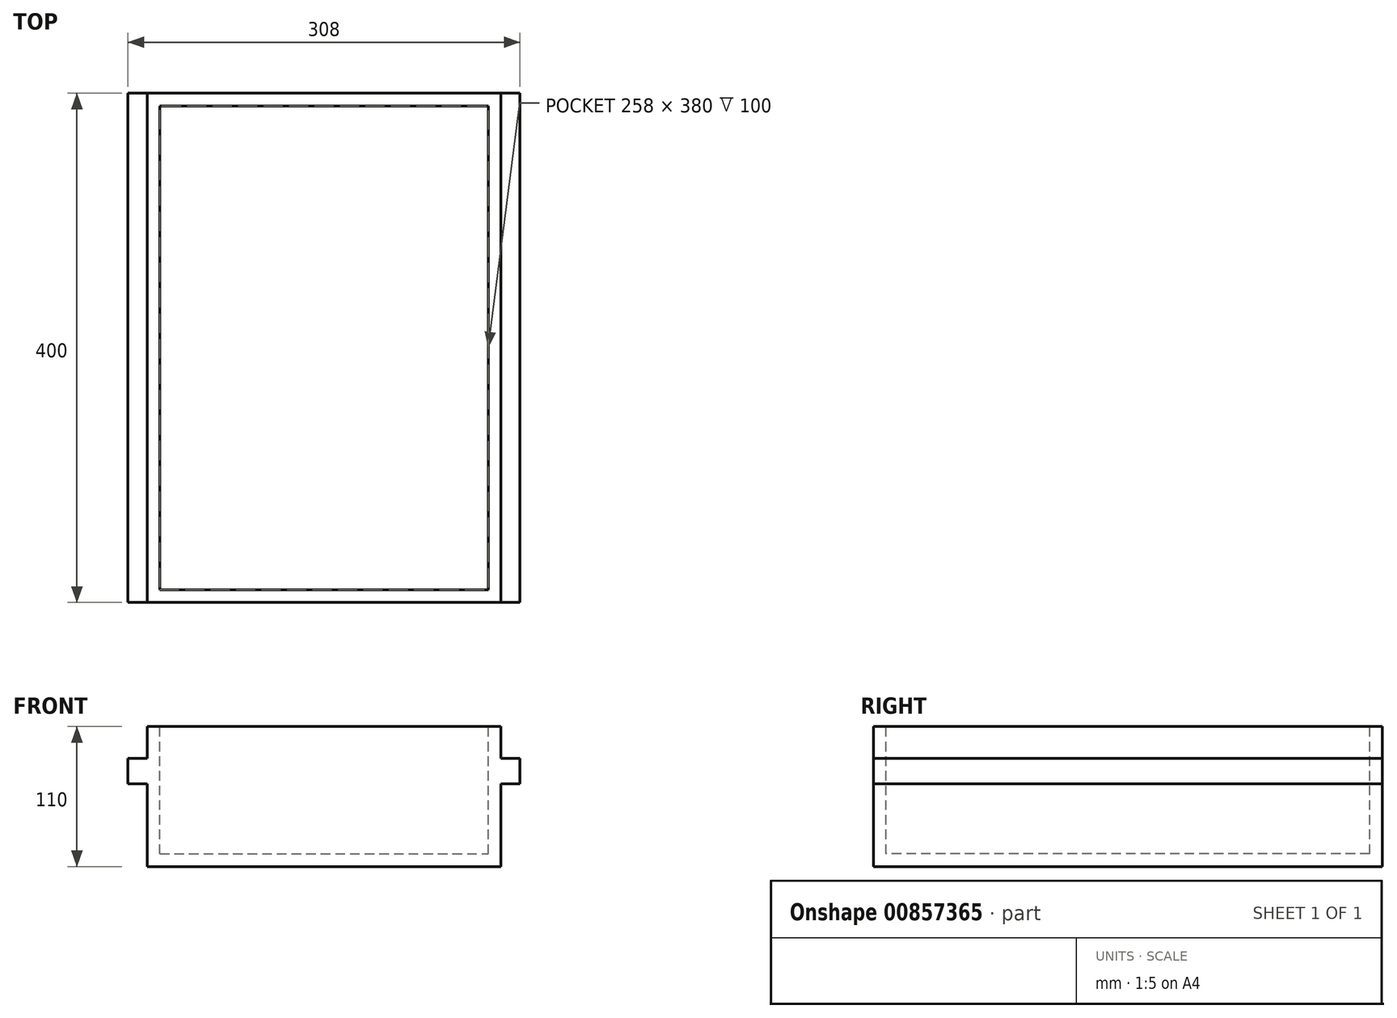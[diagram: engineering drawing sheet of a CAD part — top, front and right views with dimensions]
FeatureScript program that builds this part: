
annotation { "Feature Type Name" : "Feature", "Feature Type Description" : "" }
export const myFeature = defineFeature(function(context is Context, id is Id, definition is map)
    precondition{}
    {
        {
            var Q0;
            Q0=qCreatedBy(makeId("Top.planeOp"),FACE);
            var sketch = newSketch(context, id + "F0", { "sketchPlane" : qUnion([Q0])});
            skLineSegment(sketch, "E0.bottom", {"start": v(-139, 200) * mm, "end": v(139, 200) * mm});
            skLineSegment(sketch, "E0.top", {"start": v(-139, -200) * mm, "end": v(139, -200) * mm});
            skLineSegment(sketch, "E0.left", {"start": v(-139, 200) * mm, "end": v(-139, -200) * mm});
            skLineSegment(sketch, "E0.right", {"start": v(139, 200) * mm, "end": v(139, -200) * mm});
            skSolve(sketch);
        }
        {
            var Q0;
            Q0=makeQuery(id+"F0.imprint","IMPRINT",FACE,{"disambiguationData":[TD([[makeQuery(id+"F0.imprint","IMPRINT",EDGE,{"derivedFrom":sQuery(id+"F0.wireOp",EDGE,"E0.bottom")}),-1.0]])]});
            extrude(context, id + "F1", {"entities" : qUnion([Q0]), "depth" : 110 * mm, "offsetDistance" : 25 * mm});
        }
        {
            var Q0;
            Q0=makeQuery(id+"F1.opExtrude","CAP_FACE",FACE,{"disambiguationData":[OSD([sQuery(id+"F0.wireOp",EDGE,"E0.bottom"),sQuery(id+"F0.wireOp",EDGE,"E0.top"),sQuery(id+"F0.wireOp",EDGE,"E0.left"),sQuery(id+"F0.wireOp",EDGE,"E0.right")])],"isStart":false});
            var sketch = newSketch(context, id + "F2", { "sketchPlane" : qUnion([Q0])});
            skLineSegment(sketch, "E1.bottom", {"start": v(-129, 190) * mm, "end": v(129, 190) * mm});
            skLineSegment(sketch, "E1.top", {"start": v(-129, -190) * mm, "end": v(129, -190) * mm});
            skLineSegment(sketch, "E1.left", {"start": v(-129, 190) * mm, "end": v(-129, -190) * mm});
            skLineSegment(sketch, "E1.right", {"start": v(129, 190) * mm, "end": v(129, -190) * mm});
            skSolve(sketch);
        }
        {
            var Q0;
            Q0=makeQuery(id+"F2.imprint","IMPRINT",FACE,{"disambiguationData":[TD([[makeQuery(id+"F2.imprint","IMPRINT",EDGE,{"derivedFrom":sQuery(id+"F2.wireOp",EDGE,"E1.bottom")}),-1.0]])]});
            extrude(context, id + "F3", {"entities" : qUnion([Q0]), "operationType" : NewBodyOperationType.REMOVE, "oppositeDirection" : true, "depth" : 100 * mm, "offsetDistance" : 25 * mm});
        }
        {
            var Q0;
            Q0=makeQuery(id+"F1.opExtrude","SWEPT_FACE",FACE,{"disambiguationData":[OSD([sQuery(id+"F0.wireOp",EDGE,"E0.right")])]});
            var sketch = newSketch(context, id + "F4", { "sketchPlane" : qUnion([Q0])});
            skLineSegment(sketch, "E2.bottom", {"start": v(-200, 85) * mm, "end": v(200, 85) * mm});
            skLineSegment(sketch, "E2.top", {"start": v(-200, 65) * mm, "end": v(200, 65) * mm});
            skLineSegment(sketch, "E2.left", {"start": v(-200, 85) * mm, "end": v(-200, 65) * mm});
            skLineSegment(sketch, "E2.right", {"start": v(200, 85) * mm, "end": v(200, 65) * mm});
            skSolve(sketch);
        }
        {
            var Q0;
            Q0=makeQuery(id+"F4.imprint","IMPRINT",FACE,{"disambiguationData":[TD([[makeQuery(id+"F4.imprint","IMPRINT",EDGE,{"derivedFrom":sQuery(id+"F4.wireOp",EDGE,"E2.bottom")}),-1.0]])]});
            extrude(context, id + "F5", {"entities" : qUnion([Q0]), "operationType" : NewBodyOperationType.ADD, "depth" : 15 * mm, "offsetDistance" : 25 * mm});
        }
        {
            var Q0;
            Q0=makeQuery(id+"F1.opExtrude","SWEPT_FACE",FACE,{"disambiguationData":[OSD([sQuery(id+"F0.wireOp",EDGE,"E0.left")])]});
            var sketch = newSketch(context, id + "F6", { "sketchPlane" : qUnion([Q0])});
            skLineSegment(sketch, "E3.bottom", {"start": v(200, 85) * mm, "end": v(-200, 85) * mm});
            skLineSegment(sketch, "E3.top", {"start": v(200, 65) * mm, "end": v(-200, 65) * mm});
            skLineSegment(sketch, "E3.left", {"start": v(200, 85) * mm, "end": v(200, 65) * mm});
            skLineSegment(sketch, "E3.right", {"start": v(-200, 85) * mm, "end": v(-200, 65) * mm});
            skSolve(sketch);
        }
        {
            var Q0;
            Q0=makeQuery(id+"F6.imprint","IMPRINT",FACE,{"disambiguationData":[TD([[makeQuery(id+"F6.imprint","IMPRINT",EDGE,{"derivedFrom":sQuery(id+"F6.wireOp",EDGE,"E3.bottom")}),1.0]])]});
            extrude(context, id + "F7", {"entities" : qUnion([Q0]), "operationType" : NewBodyOperationType.ADD, "depth" : 15 * mm, "offsetDistance" : 25 * mm});
        }
    });
